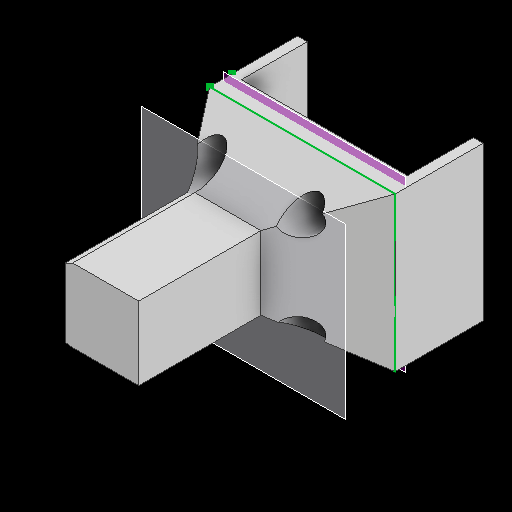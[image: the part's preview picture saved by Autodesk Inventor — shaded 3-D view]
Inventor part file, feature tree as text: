
AUTODESK INVENTOR PART (.ipt)
format: ipt  version: 2025.1 (Build 291241000, 241)  size: 231,936 bytes
history: native  units: in
note: dims shown in document units (in); Inventor stores cm internally (conversion verified against a paired STEP export)
features: sketch x13, extrude x9, other x6, projected_geometry x4, loft x1
ambient origin geometry x8: Origin, YZ Plane, XZ Plane, XY Plane, X Axis, Y Axis, Z Axis, Center Point
bodies: Body1 (feature_tree)
feature tree (33):
  other  "솔리드1"
  extrude  "돌출1"  Depth=1.4961in
  extrude  "돌출2"  Depth=1.2402in
  sketch  "스케치3"
  other  "작업 평면1"
  sketch  "스케치4"
  loft  "로프트1"
  extrude  "돌출3"  Depth=0.0787in
  sketch  "스케치7"
  other  "작업 평면2"
  sketch  "스케치8"
  sketch  "스케치9"
  sketch  "스케치10"
  extrude  "돌출4"  Depth=0.0787in
  extrude  "돌출5"  Depth=0.5315in TaperAngle=0.0deg
  extrude  "돌출6"  Depth=0.4724in
  extrude  "돌출7"  Depth=0.5906in
  extrude  "돌출8"  Depth=0.6201in
  extrude  "돌출9"  Depth=0.5906in
  sketch  "스케치1"
  sketch  "스케치2"
  projected_geometry  "투영된 루프1"
  projected_geometry  "투영된 루프2"
  sketch  "스케치5"
  other  "모서리1"
  sketch  "스케치6"
  projected_geometry  "투영된 루프3"
  other  "스케치 - 직사각형 패턴1"
  other  "스케치 - 직사각형 패턴2"
  sketch  "스케치11"
  sketch  "스케치12"
  projected_geometry  "투영된 루프4"
  sketch  "스케치13"
